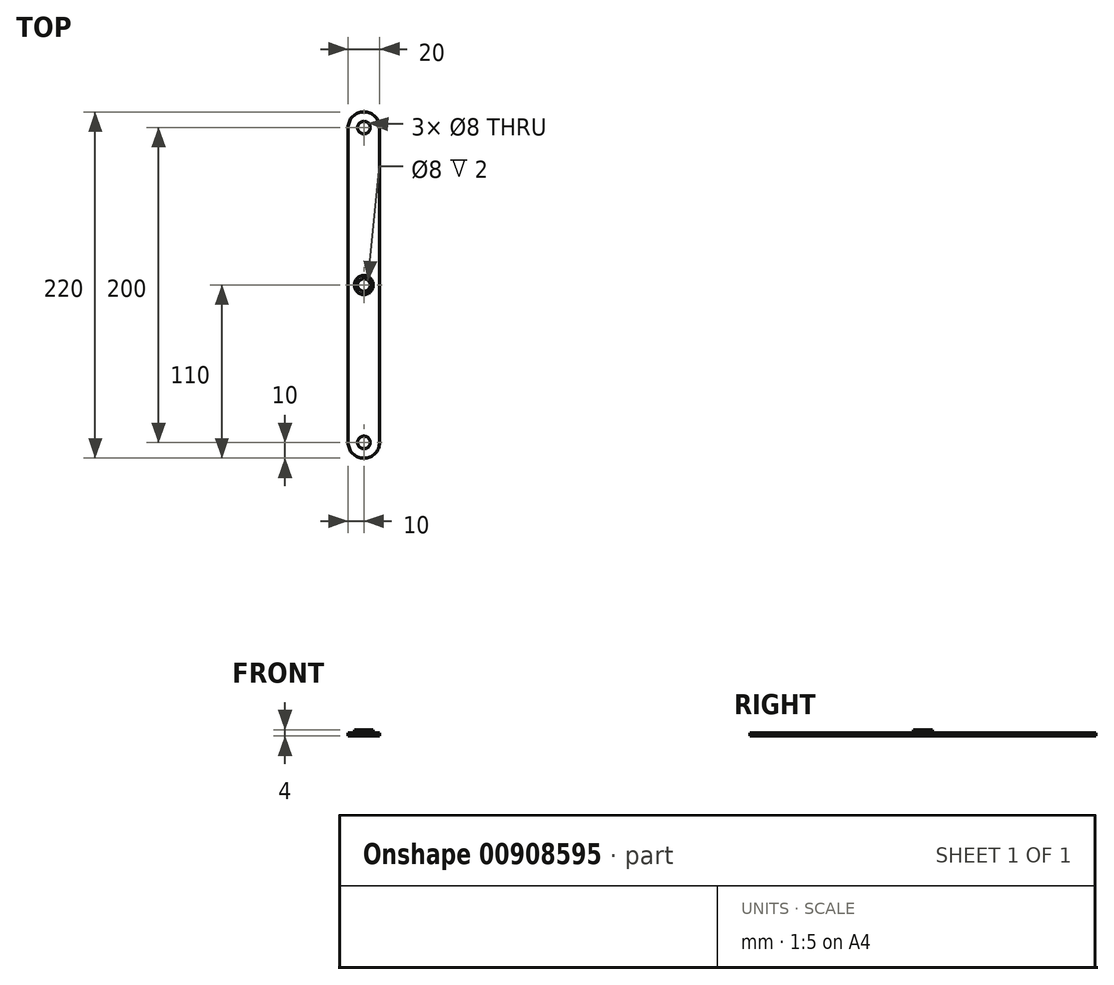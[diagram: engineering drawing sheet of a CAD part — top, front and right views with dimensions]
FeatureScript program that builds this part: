
annotation { "Feature Type Name" : "Feature", "Feature Type Description" : "" }
export const myFeature = defineFeature(function(context is Context, id is Id, definition is map)
    precondition{}
    {
        {
            var Q0;
            Q0=qCreatedBy(makeId("Top.planeOp"),FACE);
            var sketch = newSketch(context, id + "F0", { "sketchPlane" : qUnion([Q0])});
            skLineSegment(sketch, "E0.bottom", {"start": v(10, 100) * mm, "end": v(-10, 100) * mm});
            skLineSegment(sketch, "E0.top", {"start": v(10, -100) * mm, "end": v(-10, -100) * mm});
            skLineSegment(sketch, "E0.left", {"start": v(10, 100) * mm, "end": v(10, -100) * mm});
            skLineSegment(sketch, "E0.right", {"start": v(-10, 100) * mm, "end": v(-10, -100) * mm});
            skPoint(sketch, "E0.middle", {"position": v(0, 0) * mm});
            skArc(sketch, "E1", {"start": v(-10, 100) * mm, "mid": v(0, 110) * mm, "end": v(10, 100) * mm});
            skArc(sketch, "E2.MirrorCS", {"start": v(-10, -100) * mm, "mid": v(0, -110) * mm, "end": v(10, -100) * mm});
            skSolve(sketch);
        }
        {
            var Q0;
            Q0 = qSketchRegion(id + "F0", true);
            extrude(context, id + "F1", {"entities" : qUnion([Q0]), "depth" : 2 * mm, "offsetDistance" : 25 * mm});
        }
        {
            var Q0;
            Q0=qCreatedBy(makeId("Top.planeOp"),FACE);
            var sketch = newSketch(context, id + "F2", { "sketchPlane" : qUnion([Q0])});
            skCircle(sketch, "E3", {"center": v(0, 100) * mm, "radius": 4 * mm});
            skCircle(sketch, "E4", {"center": v(0, 0) * mm, "radius": 4 * mm});
            skCircle(sketch, "E5.MirrorC", {"center": v(0, -100) * mm, "radius": 4 * mm});
            skSolve(sketch);
        }
        {
            var Q0;
            Q0 = qSketchRegion(id + "F2", true);
            extrude(context, id + "F3", {"entities" : qUnion([Q0]), "operationType" : NewBodyOperationType.REMOVE, "endBound" : BoundingType.SYMMETRIC, "depth" : 25 * mm, "offsetDistance" : 25 * mm});
        }
        {
            var Q0;
            Q0=makeQuery(id+"F1.opExtrude","CAP_FACE",FACE,{"disambiguationData":[OSD([sQuery(id+"F0.wireOp",EDGE,"E0.left"),sQuery(id+"F0.wireOp",EDGE,"E0.right"),sQuery(id+"F0.wireOp",EDGE,"E1"),sQuery(id+"F0.wireOp",EDGE,"E2.MirrorCS")])],"isStart":false});
            var sketch = newSketch(context, id + "F4", { "sketchPlane" : qUnion([Q0])});
            skCircle(sketch, "E6", {"center": v(0, 0) * mm, "radius": 6 * mm});
            skCircle(sketch, "E7.0", {"center": v(0, 0) * mm, "radius": 4 * mm});
            skSolve(sketch);
        }
        {
            var Q0;
            Q0 = qSketchRegion(id + "F4", true);
            extrude(context, id + "F5", {"entities" : qUnion([Q0]), "depth" : 2 * mm, "offsetDistance" : 25 * mm});
        }
    });
